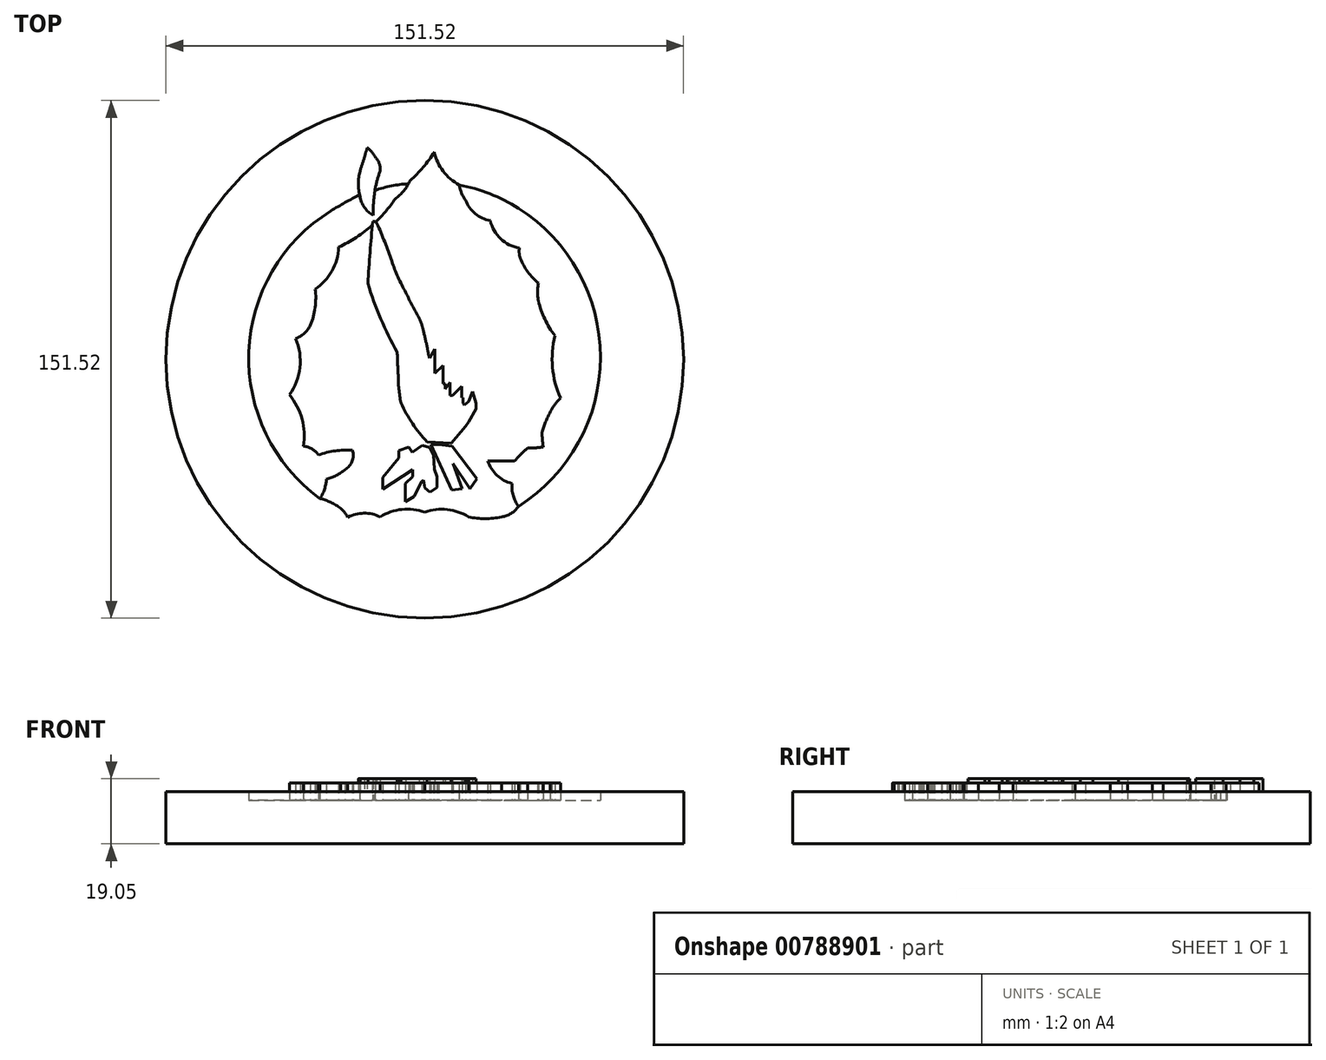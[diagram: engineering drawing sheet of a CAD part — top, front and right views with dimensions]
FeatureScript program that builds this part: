
annotation { "Feature Type Name" : "Feature", "Feature Type Description" : "" }
export const myFeature = defineFeature(function(context is Context, id is Id, definition is map)
    precondition{}
    {
        {
            var Q0;
            Q0=qCreatedBy(makeId("Top.planeOp"),FACE);
            var sketch = newSketch(context, id + "F0", { "sketchPlane" : qUnion([Q0])});
            skCircle(sketch, "E0", {"center": v(0, 0) * mm, "radius": 75.76 * mm});
            skArc(sketch, "E1", {"start": v(-13.09, -46.09) * mm, "mid": v(-17.84, -45.03) * mm, "end": v(-22.57, -46.21) * mm});
            skArc(sketch, "E2", {"start": v(0, -44.7) * mm, "mid": v(-6.7, -43.93) * mm, "end": v(-13.09, -46.09) * mm});
            skArc(sketch, "E3", {"start": v(12.84, -46.09) * mm, "mid": v(6.57, -43.97) * mm, "end": v(0, -44.7) * mm});
            skArc(sketch, "E4", {"start": v(27.38, 44.21) * mm, "mid": v(19.04, 48.43) * mm, "end": v(10.06, 51.04) * mm});
            skArc(sketch, "E5", {"start": v(-8.66, 47) * mm, "mid": v(-6.15, 49.35) * mm, "end": v(-4.36, 52.3) * mm});
            skArc(sketch, "E6", {"start": v(-25.23, 32.83) * mm, "mid": v(-20.05, 35.7) * mm, "end": v(-15.34, 39.31) * mm});
            skArc(sketch, "E7", {"start": v(-32.06, 20.56) * mm, "mid": v(-27.15, 25.87) * mm, "end": v(-25.23, 32.83) * mm});
            skArc(sketch, "E8", {"start": v(-33.48, 9.96) * mm, "mid": v(-32.12, 15.17) * mm, "end": v(-32.06, 20.56) * mm});
            skArc(sketch, "E9", {"start": v(-37.84, 6.02) * mm, "mid": v(-35.3, 7.6) * mm, "end": v(-33.48, 9.96) * mm});
            skArc(sketch, "E10", {"start": v(-39.65, -10.35) * mm, "mid": v(-36.54, -2.4) * mm, "end": v(-37.84, 6.02) * mm});
            skArc(sketch, "E11", {"start": v(-35.5, -25.45) * mm, "mid": v(-35.95, -17.46) * mm, "end": v(-39.65, -10.35) * mm});
            skArc(sketch, "E12", {"start": v(-31.14, -28) * mm, "mid": v(-33.03, -26.23) * mm, "end": v(-35.5, -25.45) * mm});
            skArc(sketch, "E13", {"start": v(-21.14, -26.62) * mm, "mid": v(-26.21, -26.8) * mm, "end": v(-31.14, -28) * mm});
            skArc(sketch, "E14", {"start": v(-23.38, -32.26) * mm, "mid": v(-21.28, -29.83) * mm, "end": v(-21.14, -26.62) * mm});
            skArc(sketch, "E15", {"start": v(-28.8, -35.03) * mm, "mid": v(-25.92, -33.97) * mm, "end": v(-23.38, -32.26) * mm});
            skArc(sketch, "E16", {"start": v(-30.71, -40.77) * mm, "mid": v(-29.37, -38.02) * mm, "end": v(-28.8, -35.03) * mm});
            skArc(sketch, "E17", {"start": v(-24.65, -43.64) * mm, "mid": v(-27.52, -41.85) * mm, "end": v(-30.71, -40.77) * mm});
            skArc(sketch, "E18", {"start": v(-22.57, -46.21) * mm, "mid": v(-23.48, -44.82) * mm, "end": v(-24.65, -43.64) * mm});
            skArc(sketch, "E19", {"start": v(12.84, -46.09) * mm, "mid": v(17.65, -46.65) * mm, "end": v(22.46, -46.09) * mm});
            skArc(sketch, "E20", {"start": v(22.46, -46.09) * mm, "mid": v(25.24, -45.1) * mm, "end": v(27.38, -43.05) * mm});
            skArc(sketch, "E21", {"start": v(25.5, -36.33) * mm, "mid": v(25.87, -39.85) * mm, "end": v(27.38, -43.05) * mm});
            skArc(sketch, "E22", {"start": v(18.48, -29.76) * mm, "mid": v(21.14, -33.96) * mm, "end": v(25.5, -36.33) * mm});
            skArc(sketch, "E23", {"start": v(26.35, -29.76) * mm, "mid": v(22.42, -29.7) * mm, "end": v(18.48, -29.76) * mm});
            skArc(sketch, "E24", {"start": v(30.06, -25.96) * mm, "mid": v(28.12, -27.77) * mm, "end": v(26.35, -29.76) * mm});
            skArc(sketch, "E25", {"start": v(30.06, -25.96) * mm, "mid": v(32.37, -25.9) * mm, "end": v(34.67, -25.65) * mm});
            skArc(sketch, "E26", {"start": v(34.26, -20.82) * mm, "mid": v(34.4, -23.24) * mm, "end": v(34.67, -25.65) * mm});
            skArc(sketch, "E27", {"start": v(36.72, -15.36) * mm, "mid": v(35.38, -18.35) * mm, "end": v(34.3, -21.44) * mm});
            skArc(sketch, "E28", {"start": v(39.72, -11.34) * mm, "mid": v(38.07, -13.24) * mm, "end": v(36.72, -15.36) * mm});
            skArc(sketch, "E29", {"start": v(38.1, 6.9) * mm, "mid": v(37.38, -2.35) * mm, "end": v(39.72, -11.34) * mm});
            skArc(sketch, "E30", {"start": v(33.27, 17.1) * mm, "mid": v(35.13, 11.73) * mm, "end": v(38.1, 6.9) * mm});
            skArc(sketch, "E31", {"start": v(33.27, 22.28) * mm, "mid": v(33.03, 19.68) * mm, "end": v(33.27, 17.1) * mm});
            skArc(sketch, "E32", {"start": v(27.96, 29.52) * mm, "mid": v(30.16, 25.56) * mm, "end": v(33.27, 22.28) * mm});
            skArc(sketch, "E33", {"start": v(27.67, 32.61) * mm, "mid": v(27.64, 31.05) * mm, "end": v(27.96, 29.52) * mm});
            skArc(sketch, "E34", {"start": v(19.17, 40.58) * mm, "mid": v(22.2, 35.3) * mm, "end": v(27.67, 32.61) * mm});
            skArc(sketch, "E35", {"start": v(11.93, 46.59) * mm, "mid": v(14.77, 42.65) * mm, "end": v(19.17, 40.58) * mm});
            skArc(sketch, "E36", {"start": v(10.06, 51.04) * mm, "mid": v(10.74, 48.7) * mm, "end": v(11.93, 46.59) * mm});
            skArc(sketch, "E37", {"start": v(2.76, 60.69) * mm, "mid": v(5.36, 55.07) * mm, "end": v(10.06, 51.04) * mm});
            skArc(sketch, "E38", {"start": v(-4.36, 52.3) * mm, "mid": v(-0.47, 56.22) * mm, "end": v(2.76, 60.69) * mm});
            skArc(sketch, "E39", {"start": v(-9.7, 28.78) * mm, "mid": v(-11.72, 34.34) * mm, "end": v(-14.03, 39.79) * mm});
            skArc(sketch, "E40", {"start": v(-9.7, 28.78) * mm, "mid": v(-7.85, 24.06) * mm, "end": v(-5.56, 19.55) * mm});
            skArc(sketch, "E41", {"start": v(-5.56, 19.55) * mm, "mid": v(-3.68, 15.76) * mm, "end": v(-1.64, 12.05) * mm});
            skArc(sketch, "E42", {"start": v(-0.4, 8.35) * mm, "mid": v(-0.91, 10.24) * mm, "end": v(-1.64, 12.05) * mm});
            skArc(sketch, "E43", {"start": v(0.73, 3.36) * mm, "mid": v(0.18, 5.86) * mm, "end": v(-0.4, 8.35) * mm});
            skArc(sketch, "E44", {"start": v(0.73, 3.36) * mm, "mid": v(1, 1.85) * mm, "end": v(1.36, 0.35) * mm});
            skLineSegment(sketch, "E45", {"start": v(1.36, 0.35) * mm, "end": v(2.88, 3.01) * mm});
            skLineSegment(sketch, "E46", {"start": v(2.88, 3.01) * mm, "end": v(2.88, -4.06) * mm});
            skLineSegment(sketch, "E47", {"start": v(5.96, -8.63) * mm, "end": v(5.96, -7.14) * mm});
            skLineSegment(sketch, "E48", {"start": v(5.96, -7.14) * mm, "end": v(5.3, -7.14) * mm});
            skLineSegment(sketch, "E49", {"start": v(5.3, -7.14) * mm, "end": v(5.3, -1.77) * mm});
            skLineSegment(sketch, "E50", {"start": v(5.3, -1.77) * mm, "end": v(2.88, -4.06) * mm});
            skLineSegment(sketch, "E51", {"start": v(5.96, -8.63) * mm, "end": v(7.32, -6.82) * mm});
            skLineSegment(sketch, "E52", {"start": v(7.32, -6.82) * mm, "end": v(7.32, -10.63) * mm});
            skLineSegment(sketch, "E53", {"start": v(7.32, -10.63) * mm, "end": v(8.17, -10.63) * mm});
            skLineSegment(sketch, "E54", {"start": v(10.78, -7.86) * mm, "end": v(8.17, -10.63) * mm});
            skLineSegment(sketch, "E55", {"start": v(10.78, -7.86) * mm, "end": v(10.78, -11.21) * mm});
            skLineSegment(sketch, "E56", {"start": v(10.78, -11.21) * mm, "end": v(11.15, -11.21) * mm});
            skLineSegment(sketch, "E57", {"start": v(11.15, -11.21) * mm, "end": v(11.15, -12.89) * mm});
            skLineSegment(sketch, "E58", {"start": v(11.15, -12.89) * mm, "end": v(11.52, -13.36) * mm});
            skLineSegment(sketch, "E59", {"start": v(11.52, -13.36) * mm, "end": v(12.83, -12.34) * mm});
            skLineSegment(sketch, "E60", {"start": v(12.83, -12.34) * mm, "end": v(14.02, -9.4) * mm});
            skLineSegment(sketch, "E61", {"start": v(14.02, -9.4) * mm, "end": v(15, -12.91) * mm});
            skLineSegment(sketch, "E62", {"start": v(15, -12.91) * mm, "end": v(15, -14.53) * mm});
            skLineSegment(sketch, "E63", {"start": v(15, -14.53) * mm, "end": v(12.88, -18.34) * mm});
            skLineSegment(sketch, "E64", {"start": v(12.88, -18.34) * mm, "end": v(11.97, -19.61) * mm});
            skLineSegment(sketch, "E65", {"start": v(11.97, -19.61) * mm, "end": v(7.8, -24.5) * mm});
            skLineSegment(sketch, "E66", {"start": v(7.8, -24.5) * mm, "end": v(0.68, -24.2) * mm});
            skArc(sketch, "E67", {"start": v(-6.97, -12.78) * mm, "mid": v(-3.6, -18.8) * mm, "end": v(0.68, -24.2) * mm});
            skArc(sketch, "E68", {"start": v(-7.78, -4.57) * mm, "mid": v(-7.6, -8.7) * mm, "end": v(-6.97, -12.78) * mm});
            skArc(sketch, "E69", {"start": v(-16.67, 22.18) * mm, "mid": v(-12.9, 11.9) * mm, "end": v(-8.07, 2.07) * mm});
            skArc(sketch, "E70", {"start": v(-8.07, 2.07) * mm, "mid": v(-7.96, -1.25) * mm, "end": v(-7.78, -4.57) * mm});
            skArc(sketch, "E71", {"start": v(-15.25, 40.38) * mm, "mid": v(-16.03, 31.28) * mm, "end": v(-16.67, 22.18) * mm});
            skArc(sketch, "E72", {"start": v(-14.03, 39.79) * mm, "mid": v(-14.55, 40.25) * mm, "end": v(-15.25, 40.38) * mm});
            skArc(sketch, "E73.trimOffspring", {"start": v(-14.41, 40.17) * mm, "mid": v(-11.35, 43.42) * mm, "end": v(-8.66, 47) * mm});
            skLineSegment(sketch, "E74", {"start": v(-7.67, -28.9) * mm, "end": v(-7.67, -26.75) * mm});
            skLineSegment(sketch, "E75", {"start": v(-7.67, -26.75) * mm, "end": v(-4.7, -25.68) * mm});
            skLineSegment(sketch, "E76", {"start": v(-4.7, -25.68) * mm, "end": v(-3.62, -27.2) * mm});
            skLineSegment(sketch, "E77", {"start": v(-3.62, -27.2) * mm, "end": v(-0.74, -25.16) * mm});
            skLineSegment(sketch, "E78", {"start": v(-0.74, -25.16) * mm, "end": v(1.43, -25.78) * mm});
            skLineSegment(sketch, "E79", {"start": v(1.43, -25.78) * mm, "end": v(2.52, -27.96) * mm});
            skLineSegment(sketch, "E80", {"start": v(2.52, -27.96) * mm, "end": v(2.78, -32.14) * mm});
            skLineSegment(sketch, "E81", {"start": v(2.78, -32.14) * mm, "end": v(3.6, -34.32) * mm});
            skLineSegment(sketch, "E82", {"start": v(3.6, -34.32) * mm, "end": v(3.6, -37.44) * mm});
            skLineSegment(sketch, "E83", {"start": v(3.6, -37.44) * mm, "end": v(1.5, -38.9) * mm});
            skLineSegment(sketch, "E84", {"start": v(1.5, -38.9) * mm, "end": v(0, -37.63) * mm});
            skLineSegment(sketch, "E85", {"start": v(0, -37.63) * mm, "end": v(-0.38, -35.33) * mm});
            skLineSegment(sketch, "E86", {"start": v(-0.38, -35.33) * mm, "end": v(-0.9, -35.71) * mm});
            skLineSegment(sketch, "E87", {"start": v(-0.9, -35.71) * mm, "end": v(-3.16, -40.19) * mm});
            skLineSegment(sketch, "E88", {"start": v(-3.16, -40.19) * mm, "end": v(-5.68, -41.7) * mm});
            skLineSegment(sketch, "E89", {"start": v(-5.68, -41.7) * mm, "end": v(-5.68, -36.39) * mm});
            skLineSegment(sketch, "E90", {"start": v(-5.68, -36.39) * mm, "end": v(-3.58, -34.32) * mm});
            skLineSegment(sketch, "E91", {"start": v(-3.58, -34.32) * mm, "end": v(-3.58, -32.25) * mm});
            skLineSegment(sketch, "E92", {"start": v(-3.58, -32.25) * mm, "end": v(-12.34, -38.04) * mm});
            skLineSegment(sketch, "E93", {"start": v(-12.34, -38.04) * mm, "end": v(-12.34, -34.54) * mm});
            skLineSegment(sketch, "E94", {"start": v(-12.34, -34.54) * mm, "end": v(-7.67, -28.9) * mm});
            skLineSegment(sketch, "E95", {"start": v(-0.74, -25.16) * mm, "end": v(-1.13, -27.5) * mm});
            skLineSegment(sketch, "E96", {"start": v(-1.13, -27.5) * mm, "end": v(-1.13, -30.07) * mm});
            skLineSegment(sketch, "E97", {"start": v(-1.13, -30.07) * mm, "end": v(-0.74, -32.02) * mm});
            skLineSegment(sketch, "E98", {"start": v(-0.74, -32.02) * mm, "end": v(0, -34.13) * mm});
            skLineSegment(sketch, "E99", {"start": v(0, -34.13) * mm, "end": v(-0.19, -36.48) * mm});
            skLineSegment(sketch, "E100", {"start": v(1.84, -24.91) * mm, "end": v(4.06, -24.91) * mm});
            skLineSegment(sketch, "E101", {"start": v(4.06, -24.91) * mm, "end": v(8.31, -30.56) * mm});
            skLineSegment(sketch, "E102", {"start": v(8.31, -30.56) * mm, "end": v(13.28, -37.93) * mm});
            skLineSegment(sketch, "E103", {"start": v(13.28, -37.93) * mm, "end": v(15.27, -34.96) * mm});
            skLineSegment(sketch, "E104", {"start": v(15.27, -34.96) * mm, "end": v(7.97, -25.4) * mm});
            skLineSegment(sketch, "E105", {"start": v(7.97, -25.4) * mm, "end": v(4.06, -24.91) * mm});
            skLineSegment(sketch, "E106", {"start": v(1.84, -24.91) * mm, "end": v(7.94, -38.3) * mm});
            skLineSegment(sketch, "E107", {"start": v(7.94, -38.3) * mm, "end": v(10.95, -37.93) * mm});
            skLineSegment(sketch, "E108", {"start": v(10.95, -37.93) * mm, "end": v(8.31, -30.56) * mm});
            skArc(sketch, "E109", {"start": v(-14.5, 50.2) * mm, "mid": v(-14.97, 46.17) * mm, "end": v(-15.13, 42.11) * mm});
            skArc(sketch, "E110", {"start": v(-13.11, 55.1) * mm, "mid": v(-13.87, 52.67) * mm, "end": v(-14.5, 50.2) * mm});
            skArc(sketch, "E111", {"start": v(-13.11, 55.1) * mm, "mid": v(-13.3, 57.29) * mm, "end": v(-14.5, 59.14) * mm});
            skArc(sketch, "E112", {"start": v(-14.5, 59.14) * mm, "mid": v(-15.51, 60.65) * mm, "end": v(-16.83, 61.9) * mm});
            skArc(sketch, "E113", {"start": v(-18.96, 47.64) * mm, "mid": v(-17.66, 44.45) * mm, "end": v(-15.13, 42.11) * mm});
            skArc(sketch, "E114", {"start": v(-18.96, 55.1) * mm, "mid": v(-19.44, 51.37) * mm, "end": v(-18.96, 47.64) * mm});
            skArc(sketch, "E115", {"start": v(-17.64, 59.14) * mm, "mid": v(-18.32, 57.12) * mm, "end": v(-18.96, 55.1) * mm});
            skArc(sketch, "E116", {"start": v(-16.83, 61.9) * mm, "mid": v(-17.28, 60.54) * mm, "end": v(-17.64, 59.14) * mm});
            skArc(sketch, "E117", {"start": v(-27.52, 43.42) * mm, "mid": v(-51.53, 2.18) * mm, "end": v(-30.71, -40.77) * mm});
            skPoint(sketch, "E117.startSnap0", {"position": v(-27.52, -41.85) * mm});
            skArc(sketch, "E118", {"start": v(-19.1, 48.17) * mm, "mid": v(-23.35, 45.89) * mm, "end": v(-27.52, 43.42) * mm});
            skArc(sketch, "E119", {"start": v(-4.8, 51.37) * mm, "mid": v(-9.76, 50.75) * mm, "end": v(-14.6, 49.47) * mm});
            skArc(sketch, "E120", {"start": v(27.38, -43.05) * mm, "mid": v(51.42, 0.58) * mm, "end": v(27.38, 44.21) * mm});
            skSolve(sketch);
        }
        {
            var Q0;
            Q0 = qSketchRegion(id + "F0", true);
            extrude(context, id + "F1", {"entities" : qUnion([Q0]), "depth" : 15.24 * mm, "offsetDistance" : 25.4 * mm});
        }
        {
            var Q0;
            Q0=makeQuery(id+"F0.imprint","IMPRINT",FACE,{"disambiguationData":[TD([[makeQuery(id+"F0.imprint","IMPRINT",EDGE,{"derivedFrom":sQuery(id+"F0.wireOp",EDGE,"E1")}),-1.0]])]});
            extrude(context, id + "F2", {"entities" : qUnion([Q0]), "operationType" : NewBodyOperationType.ADD, "depth" : 17.78 * mm, "offsetDistance" : 25.4 * mm});
        }
        {
            var Q0;
            {var subQ9=sQuery(id+"F0.wireOp",EDGE,"E6");Q0=makeQuery(id+"F0.imprint","IMPRINT",FACE,{"disambiguationData":[TD([[makeQuery(id+"F0.imprint","IMPRINT",EDGE,{"derivedFrom":subQ9}),1.0]])]});}
            var Q1;
            Q1=makeQuery(id+"F0.imprint","IMPRINT",FACE,{"disambiguationData":[TD([[makeQuery(id+"F0.imprint","IMPRINT",EDGE,{"derivedFrom":sQuery(id+"F0.wireOp",EDGE,"E4")}),1.0]])]});
            extrude(context, id + "F3", {"entities" : qUnion([Q0, Q1]), "operationType" : NewBodyOperationType.ADD, "depth" : 12.7 * mm, "offsetDistance" : 25.4 * mm});
        }
        {
            var Q0;
            {var subQ0=sQuery(id+"F0.wireOp",EDGE,"E39");Q0=makeQuery(id+"F0.imprint","IMPRINT",FACE,{"disambiguationData":[TD([[makeQuery(id+"F0.imprint","IMPRINT",EDGE,{"derivedFrom":subQ0}),1.0]])]});}
            var Q1;
            {var subQ0=sQuery(id+"F0.wireOp",EDGE,"E110");Q1=makeQuery(id+"F0.imprint","IMPRINT",FACE,{"disambiguationData":[TD([[makeQuery(id+"F0.imprint","IMPRINT",EDGE,{"derivedFrom":subQ0}),-1.0]])]});}
            extrude(context, id + "F4", {"entities" : qUnion([Q0, Q1]), "operationType" : NewBodyOperationType.ADD, "depth" : 19.05 * mm, "offsetDistance" : 25.4 * mm});
        }
        {
            var Q0;
            Q0=makeQuery(id+"F0.imprint","IMPRINT",FACE,{"disambiguationData":[TD([[makeQuery(id+"F0.imprint","IMPRINT",EDGE,{"derivedFrom":sQuery(id+"F0.wireOp",EDGE,"E74")}),-1.0]])]});
            var Q1;
            Q1=makeQuery(id+"F0.imprint","IMPRINT",FACE,{"disambiguationData":[TD([[makeQuery(id+"F0.imprint","IMPRINT",EDGE,{"derivedFrom":sQuery(id+"F0.wireOp",EDGE,"E78")}),-1.0]])]});
            var Q2;
            Q2=makeQuery(id+"F0.imprint","IMPRINT",FACE,{"disambiguationData":[TD([[makeQuery(id+"F0.imprint","IMPRINT",EDGE,{"derivedFrom":sQuery(id+"F0.wireOp",EDGE,"E100")}),-1.0]])]});
            var Q3;
            Q3=makeQuery(id+"F0.imprint","IMPRINT",FACE,{"disambiguationData":[TD([[makeQuery(id+"F0.imprint","IMPRINT",EDGE,{"derivedFrom":sQuery(id+"F0.wireOp",EDGE,"E101")}),1.0]])]});
            extrude(context, id + "F5", {"entities" : qUnion([Q0, Q1, Q2, Q3]), "operationType" : NewBodyOperationType.ADD, "depth" : 12.7 * mm, "offsetDistance" : 25.4 * mm});
        }
    });
